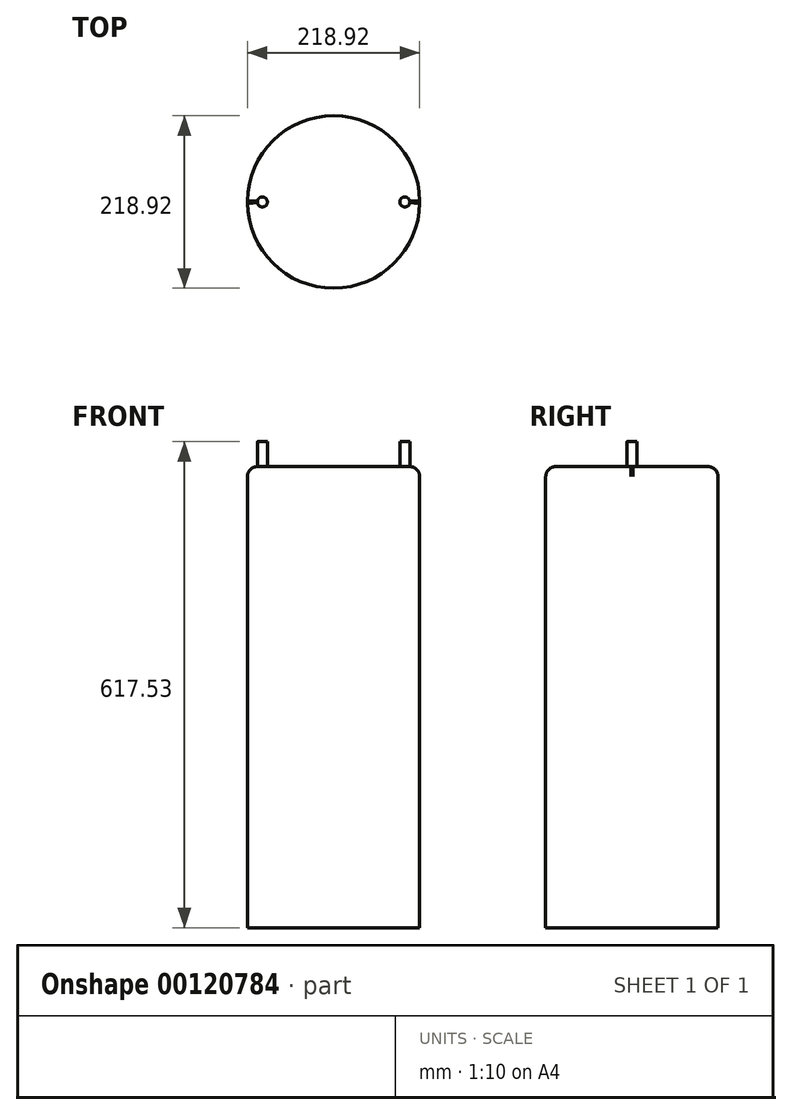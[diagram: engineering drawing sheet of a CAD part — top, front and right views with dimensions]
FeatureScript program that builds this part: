
annotation { "Feature Type Name" : "Feature", "Feature Type Description" : "" }
export const myFeature = defineFeature(function(context is Context, id is Id, definition is map)
    precondition{}
    {
        {
            var Q0;
            Q0=qCreatedBy(makeId("Top.planeOp"),FACE);
            var sketch = newSketch(context, id + "F0", { "sketchPlane" : qUnion([Q0])});
            skCircle(sketch, "E0", {"center": v(0, 0) * mm, "radius": 109.46 * mm});
            skSolve(sketch);
        }
        {
            var Q0;
            Q0=makeQuery(id+"F0.imprint","IMPRINT",FACE,{"disambiguationData":[TD([[makeQuery(id+"F0.imprint","IMPRINT",EDGE,{"derivedFrom":sQuery(id+"F0.wireOp",EDGE,"E0")}),1.0]])]});
            extrude(context, id + "F1", {"entities" : qUnion([Q0]), "endBound" : BoundingType.SYMMETRIC, "depth" : 585.8 * mm});
        }
        {
            var Q0;
            Q0=makeQuery(id+"F1.opExtrude","CAP_FACE",FACE,{"disambiguationData":[OSD([sQuery(id+"F0.wireOp",EDGE,"E0")])],"isStart":false});
            var sketch = newSketch(context, id + "F2", { "sketchPlane" : qUnion([Q0])});
            skCircle(sketch, "E1", {"center": v(90.49, 0) * mm, "radius": 6.35 * mm});
            skLineSegment(sketch, "E2", {"start": v(0, 0) * mm, "end": v(0, 19.83) * mm});
            skCircle(sketch, "E3.MirrorC", {"center": v(-90.49, 0) * mm, "radius": 6.35 * mm});
            skSolve(sketch);
        }
        {
            var Q0;
            Q0 = qSketchRegion(id + "F2", true);
            extrude(context, id + "F3", {"entities" : qUnion([Q0]), "operationType" : NewBodyOperationType.ADD, "depth" : 31.75 * mm});
        }
        {
            var Q0;
            Q0=makeQuery(id+"F1.opExtrude","CAP_EDGE",EDGE,{"disambiguationData":[OSD([sQuery(id+"F0.wireOp",EDGE,"E0")])],"isStart":false});
            fillet(context, id + "F4", {"entities" : qUnion([Q0]), "radius" : 12.7 * mm, "tangentPropagation" : true, "allowEdgeOverflow" : false});
        }
    });
